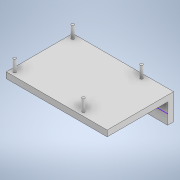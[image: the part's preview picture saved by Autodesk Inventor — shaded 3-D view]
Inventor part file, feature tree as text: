
AUTODESK INVENTOR PART (.ipt)
format: ipt  version: 2022 (Build 260153000, 153)  size: 137,728 bytes
history: native  units: mm
features: sketch x7, extrude x3, other x1, hole x1
ambient origin geometry x8: Origin, YZ Plane, XZ Plane, XY Plane, X Axis, Y Axis, Z Axis, Center Point
bodies: Body1 (feature_tree)
feature tree (12):
  other  "솔리드1"
  sketch  "스케치1"
  extrude  "돌출1"  Depth=85.0mm
  extrude  "돌출2"  Depth=56.0mm
  sketch  "스케치4"
  extrude  "돌출3"  Depth=5.0mm TaperAngle=0.0deg
  sketch  "스케치6"
  hole  "구멍1"  [1 undecoded]
  sketch  "스케치2"
  sketch  "스케치3"
  sketch  "스케치5"
  sketch  "스케치7"
note: 1 required parameter value undecoded (feature->parameter linkage not recoverable at this tier; creation-order binding heuristic only, values carry confidence <= 0.55)
